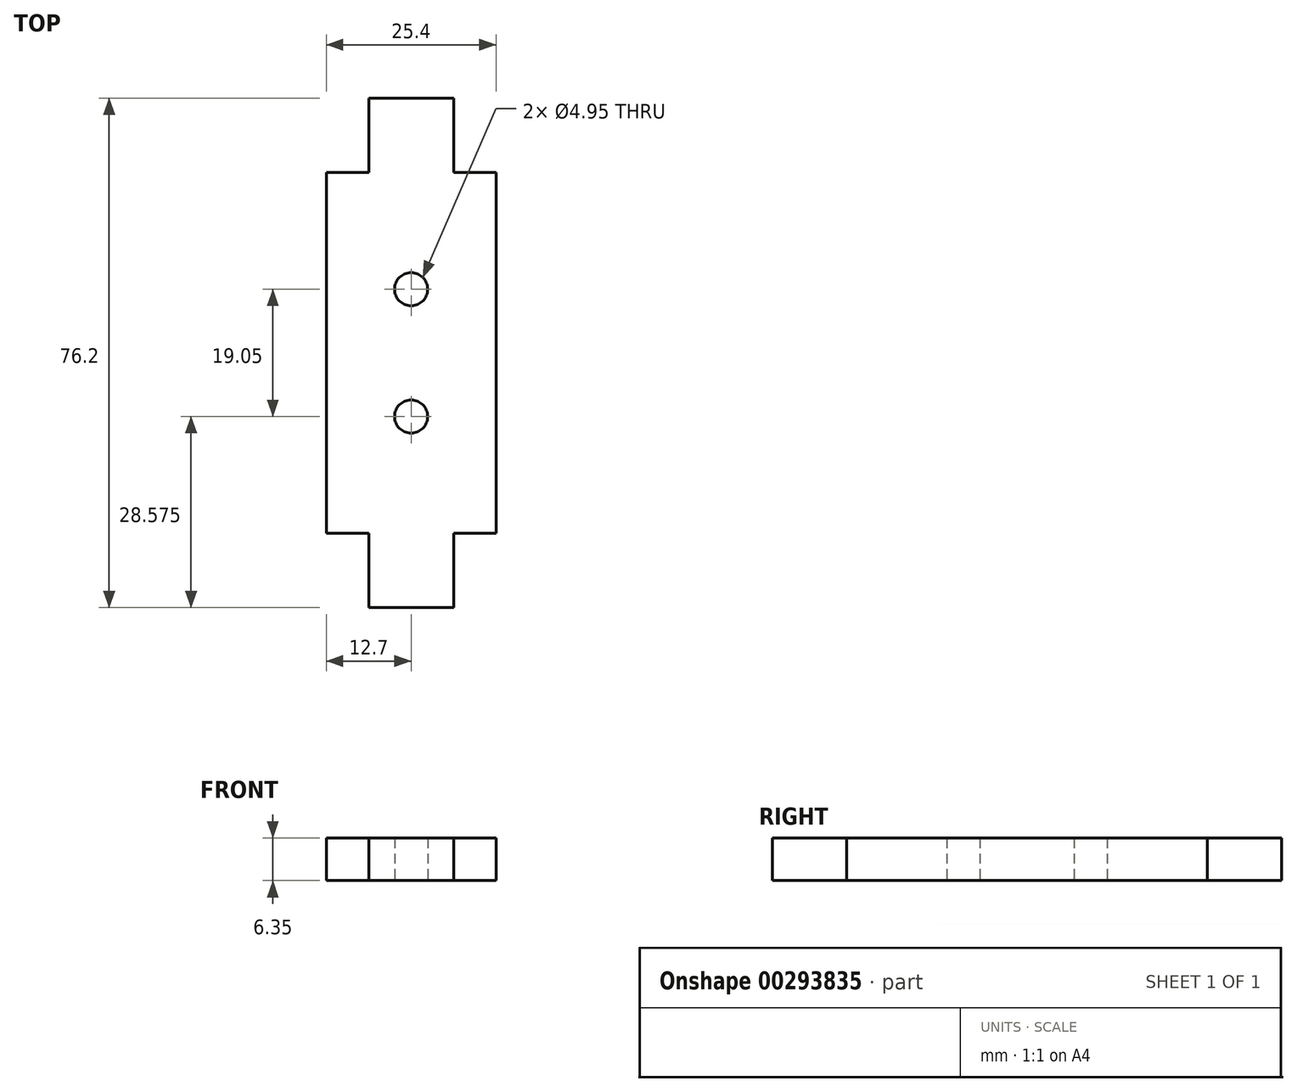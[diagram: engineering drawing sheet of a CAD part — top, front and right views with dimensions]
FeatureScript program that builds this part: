
annotation { "Feature Type Name" : "Feature", "Feature Type Description" : "" }
export const myFeature = defineFeature(function(context is Context, id is Id, definition is map)
    precondition{}
    {
        {
            var Q0;
            Q0=qCreatedBy(makeId("Top.planeOp"),FACE);
            var sketch = newSketch(context, id + "F0", { "sketchPlane" : qUnion([Q0])});
            skLineSegment(sketch, "E0", {"start": v(0, 32.54) * mm, "end": v(0, -36.18) * mm, "construction": true});
            skLineSegment(sketch, "E1", {"start": v(-39.06, 0) * mm, "end": v(39.78, 0) * mm, "construction": true});
            skLineSegment(sketch, "E2.bottom", {"start": v(-12.7, 26.99) * mm, "end": v(-6.35, 26.99) * mm});
            skLineSegment(sketch, "E2.top", {"start": v(-12.7, -26.99) * mm, "end": v(-6.35, -26.99) * mm});
            skLineSegment(sketch, "E2.left", {"start": v(-12.7, 26.99) * mm, "end": v(-12.7, -26.99) * mm});
            skLineSegment(sketch, "E2.right", {"start": v(12.7, 26.99) * mm, "end": v(12.7, -26.99) * mm});
            skPoint(sketch, "E2.middle", {"position": v(0, 0) * mm});
            skLineSegment(sketch, "E3.top", {"start": v(6.35, 38.1) * mm, "end": v(-6.35, 38.1) * mm});
            skLineSegment(sketch, "E3.left", {"start": v(6.35, 26.99) * mm, "end": v(6.35, 38.1) * mm});
            skLineSegment(sketch, "E3.right", {"start": v(-6.35, 26.99) * mm, "end": v(-6.35, 38.1) * mm});
            skPoint(sketch, "E3.middle", {"position": v(0, 32.54) * mm});
            skLineSegment(sketch, "E4.trimOffspring", {"start": v(6.35, 26.99) * mm, "end": v(12.7, 26.99) * mm});
            skLineSegment(sketch, "E5.MirrorCS", {"start": v(-6.35, -26.99) * mm, "end": v(-6.35, -38.1) * mm});
            skLineSegment(sketch, "E6.MirrorCS", {"start": v(6.35, -38.1) * mm, "end": v(-6.35, -38.1) * mm});
            skLineSegment(sketch, "E7.MirrorCS", {"start": v(6.35, -26.99) * mm, "end": v(6.35, -38.1) * mm});
            skLineSegment(sketch, "E8.MirrorCS", {"start": v(6.35, -26.99) * mm, "end": v(12.7, -26.99) * mm});
            skCircle(sketch, "E9", {"center": v(0, 9.53) * mm, "radius": 2.48 * mm});
            skCircle(sketch, "E10.MirrorC", {"center": v(0, -9.53) * mm, "radius": 2.48 * mm});
            skSolve(sketch);
        }
        {
            var Q0;
            Q0=makeQuery(id+"F0.imprint","IMPRINT",FACE,{"disambiguationData":[TD([[makeQuery(id+"F0.imprint","IMPRINT",EDGE,{"derivedFrom":sQuery(id+"F0.wireOp",EDGE,"E2.bottom")}),-1.0]])]});
            extrude(context, id + "F1", {"entities" : qUnion([Q0]), "depth" : 6.35 * mm});
        }
    });
